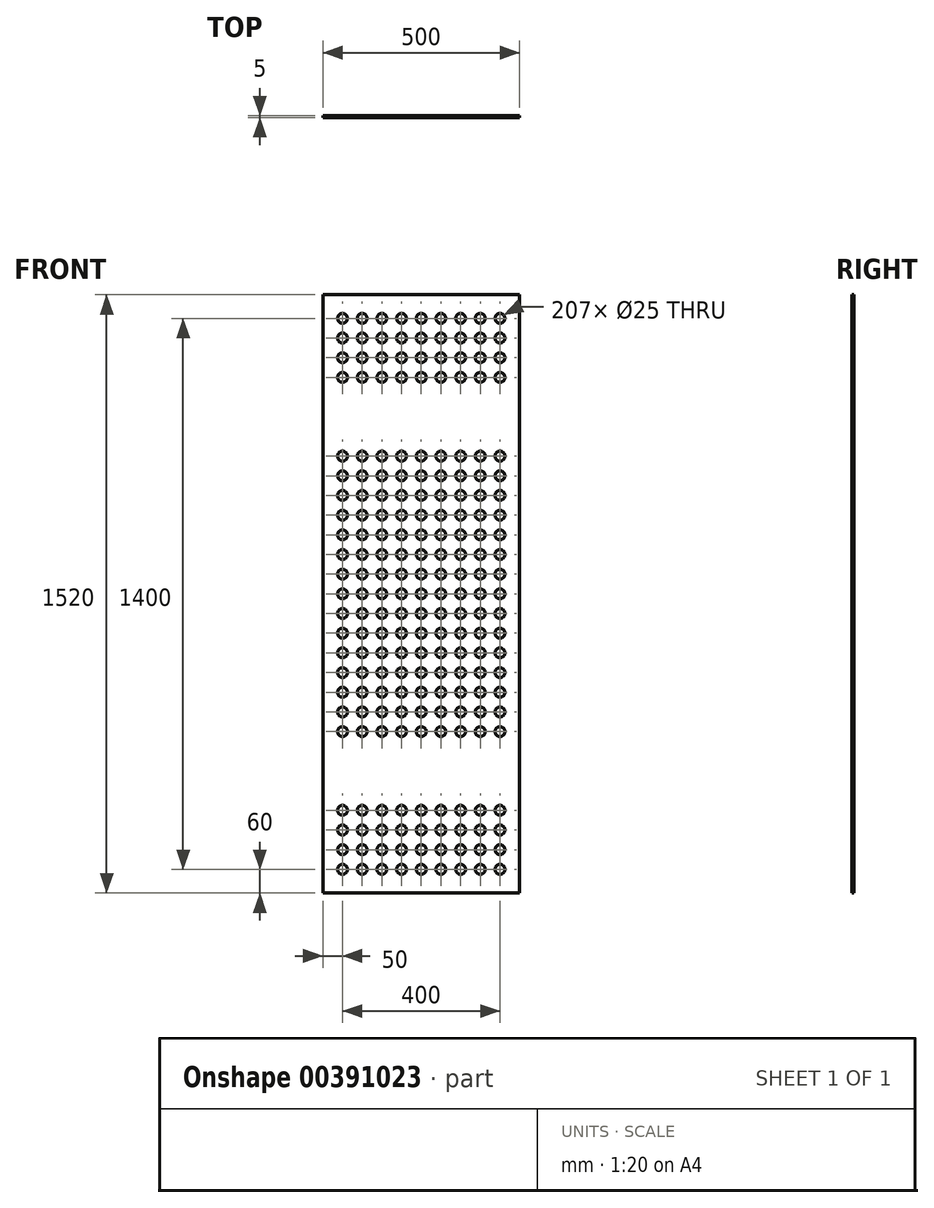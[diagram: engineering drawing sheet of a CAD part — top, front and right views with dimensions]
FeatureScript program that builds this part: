
annotation { "Feature Type Name" : "Feature", "Feature Type Description" : "" }
export const myFeature = defineFeature(function(context is Context, id is Id, definition is map)
    precondition{}
    {
        {
            var Q0;
            Q0=qCreatedBy(makeId("Front.planeOp"),FACE);
            var sketch = newSketch(context, id + "F0", { "sketchPlane" : qUnion([Q0])});
            skLineSegment(sketch, "E0.bottom", {"start": v(-250, 760) * mm, "end": v(250, 760) * mm});
            skLineSegment(sketch, "E0.top", {"start": v(-250, -760) * mm, "end": v(250, -760) * mm});
            skLineSegment(sketch, "E0.left", {"start": v(-250, 760) * mm, "end": v(-250, -760) * mm});
            skLineSegment(sketch, "E0.right", {"start": v(250, 760) * mm, "end": v(250, -760) * mm});
            skCircle(sketch, "E1", {"center": v(0, 0) * mm, "radius": 12.5 * mm});
            skCircle(sketch, "E2.0.1.0", {"center": v(0, 50) * mm, "radius": 12.5 * mm});
            skCircle(sketch, "E2.0.2.0", {"center": v(0, 100) * mm, "radius": 12.5 * mm});
            skCircle(sketch, "E2.0.3.0", {"center": v(0, 150) * mm, "radius": 12.5 * mm});
            skCircle(sketch, "E2.0.4.0", {"center": v(0, 200) * mm, "radius": 12.5 * mm});
            skCircle(sketch, "E2.0.5.0", {"center": v(0, 250) * mm, "radius": 12.5 * mm});
            skCircle(sketch, "E2.0.6.0", {"center": v(0, 300) * mm, "radius": 12.5 * mm});
            skCircle(sketch, "E2.0.7.0", {"center": v(0, 350) * mm, "radius": 12.5 * mm});
            skCircle(sketch, "E2.0.11.0", {"center": v(0, 550) * mm, "radius": 12.5 * mm});
            skCircle(sketch, "E2.0.12.0", {"center": v(0, 600) * mm, "radius": 12.5 * mm});
            skCircle(sketch, "E2.0.13.0", {"center": v(0, 650) * mm, "radius": 12.5 * mm});
            skCircle(sketch, "E2.0.14.0", {"center": v(0, 700) * mm, "radius": 12.5 * mm});
            skCircle(sketch, "E2.1.0.0", {"center": v(50, 0) * mm, "radius": 12.5 * mm});
            skCircle(sketch, "E2.1.1.0", {"center": v(50, 50) * mm, "radius": 12.5 * mm});
            skCircle(sketch, "E2.1.2.0", {"center": v(50, 100) * mm, "radius": 12.5 * mm});
            skCircle(sketch, "E2.1.3.0", {"center": v(50, 150) * mm, "radius": 12.5 * mm});
            skCircle(sketch, "E2.1.4.0", {"center": v(50, 200) * mm, "radius": 12.5 * mm});
            skCircle(sketch, "E2.1.5.0", {"center": v(50, 250) * mm, "radius": 12.5 * mm});
            skCircle(sketch, "E2.1.6.0", {"center": v(50, 300) * mm, "radius": 12.5 * mm});
            skCircle(sketch, "E2.1.7.0", {"center": v(50, 350) * mm, "radius": 12.5 * mm});
            skCircle(sketch, "E2.1.11.0", {"center": v(50, 550) * mm, "radius": 12.5 * mm});
            skCircle(sketch, "E2.1.12.0", {"center": v(50, 600) * mm, "radius": 12.5 * mm});
            skCircle(sketch, "E2.1.13.0", {"center": v(50, 650) * mm, "radius": 12.5 * mm});
            skCircle(sketch, "E2.1.14.0", {"center": v(50, 700) * mm, "radius": 12.5 * mm});
            skCircle(sketch, "E2.2.0.0", {"center": v(100, 0) * mm, "radius": 12.5 * mm});
            skCircle(sketch, "E2.2.1.0", {"center": v(100, 50) * mm, "radius": 12.5 * mm});
            skCircle(sketch, "E2.2.2.0", {"center": v(100, 100) * mm, "radius": 12.5 * mm});
            skCircle(sketch, "E2.2.3.0", {"center": v(100, 150) * mm, "radius": 12.5 * mm});
            skCircle(sketch, "E2.2.4.0", {"center": v(100, 200) * mm, "radius": 12.5 * mm});
            skCircle(sketch, "E2.2.5.0", {"center": v(100, 250) * mm, "radius": 12.5 * mm});
            skCircle(sketch, "E2.2.6.0", {"center": v(100, 300) * mm, "radius": 12.5 * mm});
            skCircle(sketch, "E2.2.7.0", {"center": v(100, 350) * mm, "radius": 12.5 * mm});
            skCircle(sketch, "E2.2.11.0", {"center": v(100, 550) * mm, "radius": 12.5 * mm});
            skCircle(sketch, "E2.2.12.0", {"center": v(100, 600) * mm, "radius": 12.5 * mm});
            skCircle(sketch, "E2.2.13.0", {"center": v(100, 650) * mm, "radius": 12.5 * mm});
            skCircle(sketch, "E2.2.14.0", {"center": v(100, 700) * mm, "radius": 12.5 * mm});
            skCircle(sketch, "E2.3.0.0", {"center": v(150, 0) * mm, "radius": 12.5 * mm});
            skCircle(sketch, "E2.3.1.0", {"center": v(150, 50) * mm, "radius": 12.5 * mm});
            skCircle(sketch, "E2.3.2.0", {"center": v(150, 100) * mm, "radius": 12.5 * mm});
            skCircle(sketch, "E2.3.3.0", {"center": v(150, 150) * mm, "radius": 12.5 * mm});
            skCircle(sketch, "E2.3.4.0", {"center": v(150, 200) * mm, "radius": 12.5 * mm});
            skCircle(sketch, "E2.3.5.0", {"center": v(150, 250) * mm, "radius": 12.5 * mm});
            skCircle(sketch, "E2.3.6.0", {"center": v(150, 300) * mm, "radius": 12.5 * mm});
            skCircle(sketch, "E2.3.7.0", {"center": v(150, 350) * mm, "radius": 12.5 * mm});
            skCircle(sketch, "E2.3.11.0", {"center": v(150, 550) * mm, "radius": 12.5 * mm});
            skCircle(sketch, "E2.3.12.0", {"center": v(150, 600) * mm, "radius": 12.5 * mm});
            skCircle(sketch, "E2.3.13.0", {"center": v(150, 650) * mm, "radius": 12.5 * mm});
            skCircle(sketch, "E2.3.14.0", {"center": v(150, 700) * mm, "radius": 12.5 * mm});
            skCircle(sketch, "E2.4.0.0", {"center": v(200, 0) * mm, "radius": 12.5 * mm});
            skCircle(sketch, "E2.4.1.0", {"center": v(200, 50) * mm, "radius": 12.5 * mm});
            skCircle(sketch, "E2.4.2.0", {"center": v(200, 100) * mm, "radius": 12.5 * mm});
            skCircle(sketch, "E2.4.3.0", {"center": v(200, 150) * mm, "radius": 12.5 * mm});
            skCircle(sketch, "E2.4.4.0", {"center": v(200, 200) * mm, "radius": 12.5 * mm});
            skCircle(sketch, "E2.4.5.0", {"center": v(200, 250) * mm, "radius": 12.5 * mm});
            skCircle(sketch, "E2.4.6.0", {"center": v(200, 300) * mm, "radius": 12.5 * mm});
            skCircle(sketch, "E2.4.7.0", {"center": v(200, 350) * mm, "radius": 12.5 * mm});
            skCircle(sketch, "E2.4.11.0", {"center": v(200, 550) * mm, "radius": 12.5 * mm});
            skCircle(sketch, "E2.4.12.0", {"center": v(200, 600) * mm, "radius": 12.5 * mm});
            skCircle(sketch, "E2.4.13.0", {"center": v(200, 650) * mm, "radius": 12.5 * mm});
            skCircle(sketch, "E2.4.14.0", {"center": v(200, 700) * mm, "radius": 12.5 * mm});
            skLineSegment(sketch, "E2.direction1", {"start": v(0, 0) * mm, "end": v(50, 0) * mm, "construction": true});
            skLineSegment(sketch, "E2.direction2", {"start": v(0, 0) * mm, "end": v(0, 50) * mm, "construction": true});
            skCircle(sketch, "E3.MirrorC", {"center": v(-150, 100) * mm, "radius": 12.5 * mm});
            skCircle(sketch, "E4.MirrorC", {"center": v(-150, 150) * mm, "radius": 12.5 * mm});
            skCircle(sketch, "E5.MirrorC", {"center": v(-100, 100) * mm, "radius": 12.5 * mm});
            skCircle(sketch, "E6.MirrorC", {"center": v(-50, 100) * mm, "radius": 12.5 * mm});
            skCircle(sketch, "E7.MirrorC", {"center": v(-150, 200) * mm, "radius": 12.5 * mm});
            skCircle(sketch, "E8.MirrorC", {"center": v(-100, 150) * mm, "radius": 12.5 * mm});
            skCircle(sketch, "E9.MirrorC", {"center": v(-50, 150) * mm, "radius": 12.5 * mm});
            skCircle(sketch, "E10.MirrorC", {"center": v(-150, 250) * mm, "radius": 12.5 * mm});
            skCircle(sketch, "E11.MirrorC", {"center": v(-100, 200) * mm, "radius": 12.5 * mm});
            skCircle(sketch, "E12.MirrorC", {"center": v(-100, 250) * mm, "radius": 12.5 * mm});
            skCircle(sketch, "E13.MirrorC", {"center": v(-50, 200) * mm, "radius": 12.5 * mm});
            skCircle(sketch, "E14.MirrorC", {"center": v(-50, 250) * mm, "radius": 12.5 * mm});
            skCircle(sketch, "E15.MirrorC", {"center": v(-150, 550) * mm, "radius": 12.5 * mm});
            skCircle(sketch, "E16.MirrorC", {"center": v(-100, 550) * mm, "radius": 12.5 * mm});
            skCircle(sketch, "E17.MirrorC", {"center": v(-150, 600) * mm, "radius": 12.5 * mm});
            skCircle(sketch, "E18.MirrorC", {"center": v(-50, 600) * mm, "radius": 12.5 * mm});
            skCircle(sketch, "E19.MirrorC", {"center": v(-50, 550) * mm, "radius": 12.5 * mm});
            skCircle(sketch, "E20.MirrorC", {"center": v(-100, 600) * mm, "radius": 12.5 * mm});
            skCircle(sketch, "E21.MirrorC", {"center": v(-50, 0) * mm, "radius": 12.5 * mm});
            skCircle(sketch, "E22.MirrorC", {"center": v(-200, 150) * mm, "radius": 12.5 * mm});
            skCircle(sketch, "E23.MirrorC", {"center": v(-100, 50) * mm, "radius": 12.5 * mm});
            skCircle(sketch, "E24.MirrorC", {"center": v(-50, 700) * mm, "radius": 12.5 * mm});
            skCircle(sketch, "E25.MirrorC", {"center": v(-150, 0) * mm, "radius": 12.5 * mm});
            skCircle(sketch, "E26.MirrorC", {"center": v(-200, 50) * mm, "radius": 12.5 * mm});
            skCircle(sketch, "E27.MirrorC", {"center": v(-50, 50) * mm, "radius": 12.5 * mm});
            skCircle(sketch, "E28.MirrorC", {"center": v(-200, 100) * mm, "radius": 12.5 * mm});
            skCircle(sketch, "E29.MirrorC", {"center": v(-150, 50) * mm, "radius": 12.5 * mm});
            skCircle(sketch, "E30.MirrorC", {"center": v(-200, 200) * mm, "radius": 12.5 * mm});
            skCircle(sketch, "E31.MirrorC", {"center": v(-100, 0) * mm, "radius": 12.5 * mm});
            skCircle(sketch, "E32.MirrorC", {"center": v(-200, 250) * mm, "radius": 12.5 * mm});
            skCircle(sketch, "E33.MirrorC", {"center": v(-200, 300) * mm, "radius": 12.5 * mm});
            skCircle(sketch, "E34.MirrorC", {"center": v(-150, 300) * mm, "radius": 12.5 * mm});
            skCircle(sketch, "E35.MirrorC", {"center": v(-200, 350) * mm, "radius": 12.5 * mm});
            skCircle(sketch, "E36.MirrorC", {"center": v(-150, 350) * mm, "radius": 12.5 * mm});
            skCircle(sketch, "E37.MirrorC", {"center": v(-100, 300) * mm, "radius": 12.5 * mm});
            skCircle(sketch, "E38.MirrorC", {"center": v(-100, 350) * mm, "radius": 12.5 * mm});
            skCircle(sketch, "E39.MirrorC", {"center": v(-50, 300) * mm, "radius": 12.5 * mm});
            skCircle(sketch, "E40.MirrorC", {"center": v(-50, 650) * mm, "radius": 12.5 * mm});
            skCircle(sketch, "E41.MirrorC", {"center": v(-200, 0) * mm, "radius": 12.5 * mm});
            skCircle(sketch, "E42.MirrorC", {"center": v(-100, 700) * mm, "radius": 12.5 * mm});
            skCircle(sketch, "E43.MirrorC", {"center": v(-200, 600) * mm, "radius": 12.5 * mm});
            skCircle(sketch, "E44.MirrorC", {"center": v(-200, 650) * mm, "radius": 12.5 * mm});
            skCircle(sketch, "E45.MirrorC", {"center": v(-200, 550) * mm, "radius": 12.5 * mm});
            skCircle(sketch, "E46.MirrorC", {"center": v(-100, 650) * mm, "radius": 12.5 * mm});
            skCircle(sketch, "E47.MirrorC", {"center": v(-150, 700) * mm, "radius": 12.5 * mm});
            skCircle(sketch, "E48.MirrorC", {"center": v(-50, 350) * mm, "radius": 12.5 * mm});
            skCircle(sketch, "E49.MirrorC", {"center": v(-150, 650) * mm, "radius": 12.5 * mm});
            skCircle(sketch, "E50.MirrorC", {"center": v(-200, 700) * mm, "radius": 12.5 * mm});
            skCircle(sketch, "E51.MirrorC", {"center": v(-200, -650) * mm, "radius": 12.5 * mm});
            skCircle(sketch, "E52.MirrorC", {"center": v(200, -150) * mm, "radius": 12.5 * mm});
            skCircle(sketch, "E53.MirrorC", {"center": v(-100, -100) * mm, "radius": 12.5 * mm});
            skCircle(sketch, "E54.MirrorC", {"center": v(200, -650) * mm, "radius": 12.5 * mm});
            skCircle(sketch, "E55.MirrorC", {"center": v(-150, -650) * mm, "radius": 12.5 * mm});
            skCircle(sketch, "E56.MirrorC", {"center": v(200, -550) * mm, "radius": 12.5 * mm});
            skCircle(sketch, "E57.MirrorC", {"center": v(-100, -50) * mm, "radius": 12.5 * mm});
            skCircle(sketch, "E58.MirrorC", {"center": v(-50, -700) * mm, "radius": 12.5 * mm});
            skCircle(sketch, "E59.MirrorC", {"center": v(200, -600) * mm, "radius": 12.5 * mm});
            skCircle(sketch, "E60.MirrorC", {"center": v(-200, -50) * mm, "radius": 12.5 * mm});
            skCircle(sketch, "E61.MirrorC", {"center": v(-50, -650) * mm, "radius": 12.5 * mm});
            skCircle(sketch, "E62.MirrorC", {"center": v(-50, -50) * mm, "radius": 12.5 * mm});
            skCircle(sketch, "E63.MirrorC", {"center": v(-150, -550) * mm, "radius": 12.5 * mm});
            skCircle(sketch, "E64.MirrorC", {"center": v(-200, -150) * mm, "radius": 12.5 * mm});
            skCircle(sketch, "E65.MirrorC", {"center": v(-200, -100) * mm, "radius": 12.5 * mm});
            skCircle(sketch, "E66.MirrorC", {"center": v(200, -50) * mm, "radius": 12.5 * mm});
            skCircle(sketch, "E67.MirrorC", {"center": v(-150, -100) * mm, "radius": 12.5 * mm});
            skCircle(sketch, "E68.MirrorC", {"center": v(-50, -550) * mm, "radius": 12.5 * mm});
            skCircle(sketch, "E69.MirrorC", {"center": v(-50, -150) * mm, "radius": 12.5 * mm});
            skCircle(sketch, "E70.MirrorC", {"center": v(-50, -100) * mm, "radius": 12.5 * mm});
            skCircle(sketch, "E71.MirrorC", {"center": v(150, -150) * mm, "radius": 12.5 * mm});
            skCircle(sketch, "E72.MirrorC", {"center": v(-200, -550) * mm, "radius": 12.5 * mm});
            skCircle(sketch, "E73.MirrorC", {"center": v(-150, -600) * mm, "radius": 12.5 * mm});
            skCircle(sketch, "E74.MirrorC", {"center": v(-200, -600) * mm, "radius": 12.5 * mm});
            skCircle(sketch, "E75.MirrorC", {"center": v(200, -100) * mm, "radius": 12.5 * mm});
            skCircle(sketch, "E76.MirrorC", {"center": v(-150, -150) * mm, "radius": 12.5 * mm});
            skCircle(sketch, "E77.MirrorC", {"center": v(-150, -700) * mm, "radius": 12.5 * mm});
            skLineSegment(sketch, "E78.MirrorCS", {"start": v(0, 0) * mm, "end": v(0, -50) * mm, "construction": true});
            skCircle(sketch, "E79.MirrorC", {"center": v(-50, -600) * mm, "radius": 12.5 * mm});
            skCircle(sketch, "E80.MirrorC", {"center": v(-100, -600) * mm, "radius": 12.5 * mm});
            skCircle(sketch, "E81.MirrorC", {"center": v(-100, -150) * mm, "radius": 12.5 * mm});
            skCircle(sketch, "E82.MirrorC", {"center": v(-100, -650) * mm, "radius": 12.5 * mm});
            skCircle(sketch, "E83.MirrorC", {"center": v(-100, -550) * mm, "radius": 12.5 * mm});
            skCircle(sketch, "E84.MirrorC", {"center": v(-150, -50) * mm, "radius": 12.5 * mm});
            skCircle(sketch, "E85.MirrorC", {"center": v(150, -100) * mm, "radius": 12.5 * mm});
            skCircle(sketch, "E86.MirrorC", {"center": v(100, -50) * mm, "radius": 12.5 * mm});
            skCircle(sketch, "E87.MirrorC", {"center": v(-50, -300) * mm, "radius": 12.5 * mm});
            skCircle(sketch, "E88.MirrorC", {"center": v(100, -550) * mm, "radius": 12.5 * mm});
            skCircle(sketch, "E89.MirrorC", {"center": v(150, -600) * mm, "radius": 12.5 * mm});
            skCircle(sketch, "E90.MirrorC", {"center": v(-50, -200) * mm, "radius": 12.5 * mm});
            skCircle(sketch, "E91.MirrorC", {"center": v(150, -550) * mm, "radius": 12.5 * mm});
            skCircle(sketch, "E92.MirrorC", {"center": v(-100, -350) * mm, "radius": 12.5 * mm});
            skCircle(sketch, "E93.MirrorC", {"center": v(-50, -250) * mm, "radius": 12.5 * mm});
            skCircle(sketch, "E94.MirrorC", {"center": v(-200, -700) * mm, "radius": 12.5 * mm});
            skCircle(sketch, "E95.MirrorC", {"center": v(200, -700) * mm, "radius": 12.5 * mm});
            skCircle(sketch, "E96.MirrorC", {"center": v(150, -650) * mm, "radius": 12.5 * mm});
            skCircle(sketch, "E97.MirrorC", {"center": v(100, -600) * mm, "radius": 12.5 * mm});
            skCircle(sketch, "E98.MirrorC", {"center": v(50, -550) * mm, "radius": 12.5 * mm});
            skCircle(sketch, "E99.MirrorC", {"center": v(150, -700) * mm, "radius": 12.5 * mm});
            skCircle(sketch, "E100.MirrorC", {"center": v(100, -650) * mm, "radius": 12.5 * mm});
            skCircle(sketch, "E101.MirrorC", {"center": v(50, -600) * mm, "radius": 12.5 * mm});
            skCircle(sketch, "E102.MirrorC", {"center": v(0, -550) * mm, "radius": 12.5 * mm});
            skCircle(sketch, "E103.MirrorC", {"center": v(0, -50) * mm, "radius": 12.5 * mm});
            skCircle(sketch, "E104.MirrorC", {"center": v(-100, -250) * mm, "radius": 12.5 * mm});
            skCircle(sketch, "E105.MirrorC", {"center": v(50, -350) * mm, "radius": 12.5 * mm});
            skCircle(sketch, "E106.MirrorC", {"center": v(0, -100) * mm, "radius": 12.5 * mm});
            skCircle(sketch, "E107.MirrorC", {"center": v(0, -150) * mm, "radius": 12.5 * mm});
            skCircle(sketch, "E108.MirrorC", {"center": v(0, -200) * mm, "radius": 12.5 * mm});
            skCircle(sketch, "E109.MirrorC", {"center": v(0, -250) * mm, "radius": 12.5 * mm});
            skCircle(sketch, "E110.MirrorC", {"center": v(0, -300) * mm, "radius": 12.5 * mm});
            skCircle(sketch, "E111.MirrorC", {"center": v(0, -350) * mm, "radius": 12.5 * mm});
            skCircle(sketch, "E112.MirrorC", {"center": v(-50, -350) * mm, "radius": 12.5 * mm});
            skCircle(sketch, "E113.MirrorC", {"center": v(-100, -200) * mm, "radius": 12.5 * mm});
            skCircle(sketch, "E114.MirrorC", {"center": v(-100, -300) * mm, "radius": 12.5 * mm});
            skCircle(sketch, "E115.MirrorC", {"center": v(50, -300) * mm, "radius": 12.5 * mm});
            skCircle(sketch, "E116.MirrorC", {"center": v(100, -350) * mm, "radius": 12.5 * mm});
            skCircle(sketch, "E117.MirrorC", {"center": v(100, -250) * mm, "radius": 12.5 * mm});
            skCircle(sketch, "E118.MirrorC", {"center": v(50, -200) * mm, "radius": 12.5 * mm});
            skCircle(sketch, "E119.MirrorC", {"center": v(-200, -350) * mm, "radius": 12.5 * mm});
            skCircle(sketch, "E120.MirrorC", {"center": v(200, -350) * mm, "radius": 12.5 * mm});
            skCircle(sketch, "E121.MirrorC", {"center": v(0, -650) * mm, "radius": 12.5 * mm});
            skCircle(sketch, "E122.MirrorC", {"center": v(50, -50) * mm, "radius": 12.5 * mm});
            skCircle(sketch, "E123.MirrorC", {"center": v(200, -200) * mm, "radius": 12.5 * mm});
            skCircle(sketch, "E124.MirrorC", {"center": v(100, -100) * mm, "radius": 12.5 * mm});
            skCircle(sketch, "E125.MirrorC", {"center": v(-200, -250) * mm, "radius": 12.5 * mm});
            skCircle(sketch, "E126.MirrorC", {"center": v(-200, -200) * mm, "radius": 12.5 * mm});
            skCircle(sketch, "E127.MirrorC", {"center": v(50, -100) * mm, "radius": 12.5 * mm});
            skCircle(sketch, "E128.MirrorC", {"center": v(-150, -200) * mm, "radius": 12.5 * mm});
            skCircle(sketch, "E129.MirrorC", {"center": v(150, -50) * mm, "radius": 12.5 * mm});
            skCircle(sketch, "E130.MirrorC", {"center": v(50, -650) * mm, "radius": 12.5 * mm});
            skCircle(sketch, "E131.MirrorC", {"center": v(200, -250) * mm, "radius": 12.5 * mm});
            skCircle(sketch, "E132.MirrorC", {"center": v(100, -700) * mm, "radius": 12.5 * mm});
            skCircle(sketch, "E133.MirrorC", {"center": v(150, -200) * mm, "radius": 12.5 * mm});
            skCircle(sketch, "E134.MirrorC", {"center": v(100, -150) * mm, "radius": 12.5 * mm});
            skCircle(sketch, "E135.MirrorC", {"center": v(150, -350) * mm, "radius": 12.5 * mm});
            skCircle(sketch, "E136.MirrorC", {"center": v(100, -300) * mm, "radius": 12.5 * mm});
            skCircle(sketch, "E137.MirrorC", {"center": v(-200, -300) * mm, "radius": 12.5 * mm});
            skCircle(sketch, "E138.MirrorC", {"center": v(-150, -350) * mm, "radius": 12.5 * mm});
            skCircle(sketch, "E139.MirrorC", {"center": v(50, -250) * mm, "radius": 12.5 * mm});
            skCircle(sketch, "E140.MirrorC", {"center": v(0, -700) * mm, "radius": 12.5 * mm});
            skCircle(sketch, "E141.MirrorC", {"center": v(-150, -250) * mm, "radius": 12.5 * mm});
            skCircle(sketch, "E142.MirrorC", {"center": v(0, -600) * mm, "radius": 12.5 * mm});
            skCircle(sketch, "E143.MirrorC", {"center": v(50, -150) * mm, "radius": 12.5 * mm});
            skCircle(sketch, "E144.MirrorC", {"center": v(200, -300) * mm, "radius": 12.5 * mm});
            skCircle(sketch, "E145.MirrorC", {"center": v(150, -250) * mm, "radius": 12.5 * mm});
            skCircle(sketch, "E146.MirrorC", {"center": v(100, -200) * mm, "radius": 12.5 * mm});
            skCircle(sketch, "E147.MirrorC", {"center": v(-100, -700) * mm, "radius": 12.5 * mm});
            skCircle(sketch, "E148.MirrorC", {"center": v(-150, -300) * mm, "radius": 12.5 * mm});
            skCircle(sketch, "E149.MirrorC", {"center": v(150, -300) * mm, "radius": 12.5 * mm});
            skCircle(sketch, "E150.MirrorC", {"center": v(50, -700) * mm, "radius": 12.5 * mm});
            skSolve(sketch);
        }
        {
            var Q0;
            Q0=makeQuery(id+"F0.imprint","IMPRINT",FACE,{"disambiguationData":[TD([[makeQuery(id+"F0.imprint","IMPRINT",EDGE,{"derivedFrom":sQuery(id+"F0.wireOp",EDGE,"E0.bottom")}),-1.0]])]});
            extrude(context, id + "F1", {"entities" : qUnion([Q0]), "depth" : 5 * mm});
        }
    });
